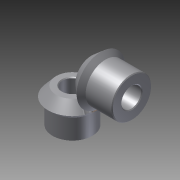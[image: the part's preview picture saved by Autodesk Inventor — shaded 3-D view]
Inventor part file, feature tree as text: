
AUTODESK INVENTOR PART (.ipt)
format: ipt  version: 2012 (Build 160160000, 160)  size: 465,408 bytes
history: native  units: in
note: dims shown in document units (in); Inventor stores cm internally (conversion verified against a paired STEP export)
features: imported_body x2, other x2, extrude x1, sketch x1
ambient origin geometry x8: Origin, YZ Plane, XZ Plane, XY Plane, X Axis, Y Axis, Z Axis, Center Point
feature tree (6):
  extrude  "Extrusion1"  [1 undecoded]
  imported_body  "Base1"
  imported_body  "Base2"
  sketch  "Sketch2"  dims[d0=0.125in d1=0.0in]
  other  "Composite1"
  other  "Srf1"
note: 1 required parameter value undecoded (feature->parameter linkage not recoverable at this tier; creation-order binding heuristic only, values carry confidence <= 0.55)
